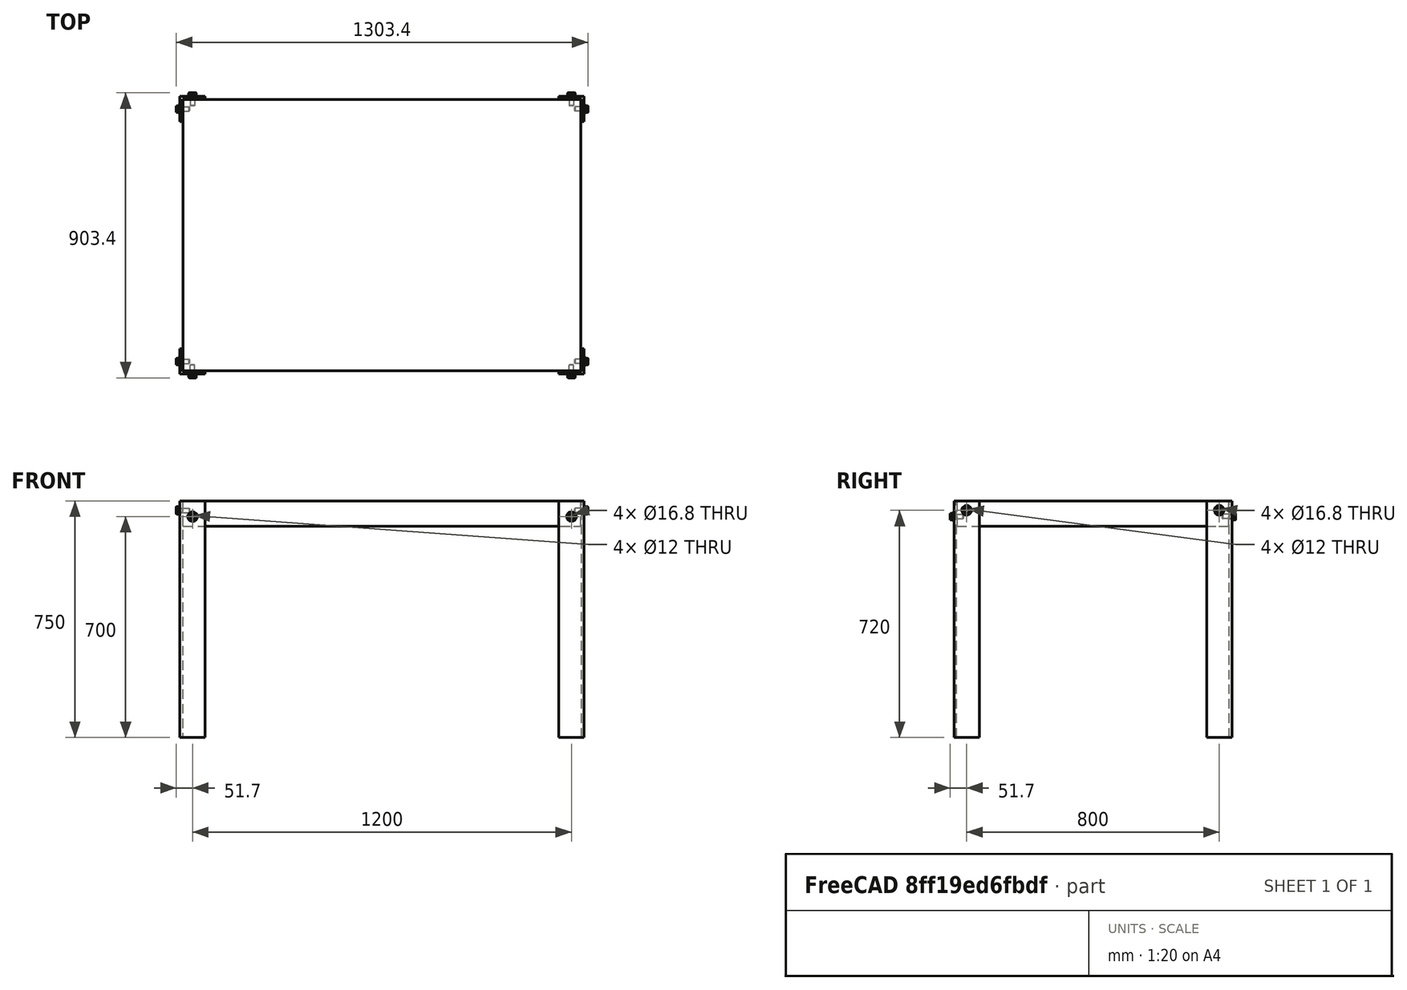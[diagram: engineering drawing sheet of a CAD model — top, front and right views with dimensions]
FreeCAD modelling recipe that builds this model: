
FCSTD DOCUMENT  (FreeCAD 0.19R24366 (Git))
Label: table_test
License: All rights reserved
LicenseURL: http://en.wikipedia.org/wiki/All_rights_reserved
objects: Part::Cut×13, Part::Box×9, Part::FeaturePython×8, Part::Cylinder×4
note: 34 computed .brp shape members not serialized (recipe doc carries the construction recipe); baked Part::Feature solids carry a one-line shape summary decoded from their .brp

FEATURE [Part::Box] Box  label="Куб"
  AttacherType = Attacher::AttachEngine3D
  Height = 750
  Length = 80
  Width = 80
FEATURE [Part::Box] Box001  label="Куб001"
  AttacherType = Attacher::AttachEngine3D
  Height = 750
  Length = 80
  Placement = pos=(8,8,0) rot=(0,0,1;0rad)
  Width = 80
FEATURE [Part::Box] Box002  label="Куб002"
  AttacherType = Attacher::AttachEngine3D
  Height = 750
  Length = 80
  Placement = pos=(0,800,0) rot=(0,0,1;0rad)
  Width = 80
FEATURE [Part::Box] Box003  label="Куб003"
  AttacherType = Attacher::AttachEngine3D
  Height = 750
  Length = 80
  Placement = pos=(8,792,0) rot=(0,0,1;0rad)
  Width = 80
FEATURE [Part::Box] Box004  label="Куб004"
  AttacherType = Attacher::AttachEngine3D
  Height = 750
  Length = 80
  Placement = pos=(1200,0,0) rot=(0,0,1;0rad)
  Width = 80
FEATURE [Part::Box] Box005  label="Куб005"
  AttacherType = Attacher::AttachEngine3D
  Height = 750
  Length = 80
  Placement = pos=(1192,8,0) rot=(0,0,1;0rad)
  Width = 80
FEATURE [Part::Box] Box006  label="Куб006"
  AttacherType = Attacher::AttachEngine3D
  Height = 750
  Length = 80
  Placement = pos=(1200,800,0) rot=(0,0,1;0rad)
  Width = 80
FEATURE [Part::Box] Box007  label="Куб007"
  AttacherType = Attacher::AttachEngine3D
  Height = 750
  Length = 80
  Placement = pos=(1192,792,0) rot=(0,0,1;0rad)
  Width = 80
FEATURE [Part::Cut] Cut
  Base = -> Box
  Tool = -> Box001
FEATURE [Part::Cut] Cut001
  Base = -> Box002
  Tool = -> Box003
FEATURE [Part::Cut] Cut002
  Base = -> Box004
  Tool = -> Box005
FEATURE [Part::Cut] Cut003
  Base = -> Box006
  Tool = -> Box007
FEATURE [Part::Cylinder] Cylinder  label="Цилиндр"
  Angle = 360
  AttacherType = Attacher::AttachEngine3D
  Height = 1300
  Placement = pos=(-10,40,720) rot=(0,1,0;1.5708rad)
  Radius = 6
FEATURE [Part::Cylinder] Cylinder001  label="Цилиндр001"
  Angle = 360
  AttacherType = Attacher::AttachEngine3D
  Height = 1300
  Placement = pos=(-10,840,720) rot=(0,1,0;1.5708rad)
  Radius = 6
FEATURE [Part::Cylinder] Cylinder002  label="Цилиндр002"
  Angle = 360
  AttacherType = Attacher::AttachEngine3D
  Height = 900
  Placement = pos=(40,-10,700) rot=(-1,0,0;1.5708rad)
  Radius = 6
FEATURE [Part::Cylinder] Cylinder003  label="Цилиндр003"
  Angle = 360
  AttacherType = Attacher::AttachEngine3D
  Height = 900
  Placement = pos=(1240,-10,700) rot=(-1,0,0;1.5708rad)
  Radius = 6
FEATURE [Part::Cut] Cut004
  Base = -> Cut
  Tool = -> Cylinder
FEATURE [Part::Cut] Cut005
  Base = -> Cut002
  Tool = -> Cylinder
FEATURE [Part::Cut] Cut006
  Base = -> Cut005
  Tool = -> Cylinder003
FEATURE [Part::Cut] Cut007
  Base = -> Cut003
  Tool = -> Cylinder003
FEATURE [Part::Cut] Cut008
  Base = -> Cut007
  Tool = -> Cylinder001
FEATURE [Part::Cut] Cut009
  Base = -> Cut001
  Tool = -> Cylinder001
FEATURE [Part::Cut] Cut010
  Base = -> Cut004
  Tool = -> Cylinder002
FEATURE [Part::Cut] Cut011
  Base = -> Cut009
  Tool = -> Cylinder001
FEATURE [Part::Cut] Cut012
  Base = -> Cut011
  Tool = -> Cylinder002
FEATURE [Part::Box] Box008  label="Столешница"
  AttacherType = Attacher::AttachEngine3D
  Height = 80
  Length = 1260
  Placement = pos=(10,10,670) rot=(0,0,1;0rad)
  Width = 860
FEATURE [Part::FeaturePython] Screw  label="(M14)x30-Screw"  # Fasteners workbench fastener (typed FeaturePython)
  Placement = pos=(40,880,700) rot=(-1,0,0;1.5708rad)
  baseObject = -> Cut012 [Edge18]
  diameter = 6
  invert = false
  length = 0
  lengthCustom = 30
  matchOuter = false
  offset = 2
  thread = false
  type = 17
FEATURE [Part::FeaturePython] Screw001  label="(M14)x30-Screw001"  # Fasteners workbench fastener (typed FeaturePython)
  Placement = pos=(0,840,720) rot=(0,-1,0;1.5708rad)
  baseObject = -> Cut012 [Edge5]
  diameter = 6
  invert = true
  length = 0
  lengthCustom = 30
  matchOuter = false
  offset = 2
  thread = false
  type = 17
FEATURE [Part::FeaturePython] Screw002  label="(M14)x30-Screw002"  # Fasteners workbench fastener (typed FeaturePython)
  Placement = pos=(0,40,720) rot=(0,-1,0;1.5708rad)
  baseObject = -> Cut010 [Edge5]
  diameter = 6
  invert = true
  length = 0
  lengthCustom = 30
  matchOuter = false
  offset = 2
  thread = false
  type = 17
FEATURE [Part::FeaturePython] Screw003  label="(M14)x30-Screw003"  # Fasteners workbench fastener (typed FeaturePython)
  Placement = pos=(1240,880,700) rot=(-1,0,0;1.5708rad)
  baseObject = -> Cut008 [Edge12]
  diameter = 6
  invert = false
  length = 0
  lengthCustom = 30
  matchOuter = false
  offset = 2
  thread = false
  type = 17
FEATURE [Part::FeaturePython] Screw004  label="(M14)x30-Screw004"  # Fasteners workbench fastener (typed FeaturePython)
  Placement = pos=(1280,840,720) rot=(0,1,0;1.5708rad)
  baseObject = -> Cut008 [Edge20]
  diameter = 6
  invert = false
  length = 0
  lengthCustom = 30
  matchOuter = false
  offset = 2
  thread = false
  type = 17
FEATURE [Part::FeaturePython] Screw005  label="(M14)x30-Screw005"  # Fasteners workbench fastener (typed FeaturePython)
  Placement = pos=(1280,40,720) rot=(0,1,0;1.5708rad)
  baseObject = -> Cut006 [Edge22]
  diameter = 6
  invert = false
  length = 0
  lengthCustom = 30
  matchOuter = false
  offset = 2
  thread = false
  type = 17
FEATURE [Part::FeaturePython] Screw006  label="(M14)x30-Screw006"  # Fasteners workbench fastener (typed FeaturePython)
  Placement = pos=(1240,0,700) rot=(1,0,0;1.5708rad)
  baseObject = -> Cut006 [Edge18]
  diameter = 6
  invert = true
  length = 0
  lengthCustom = 30
  matchOuter = false
  offset = 2
  thread = false
  type = 17
FEATURE [Part::FeaturePython] Screw007  label="(M14)x30-Screw007"  # Fasteners workbench fastener (typed FeaturePython)
  Placement = pos=(40,0,700) rot=(1,0,0;1.5708rad)
  baseObject = -> Cut010 [Edge9]
  diameter = 6
  invert = true
  length = 0
  lengthCustom = 30
  matchOuter = false
  offset = 2
  thread = false
  type = 17
